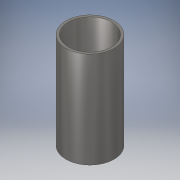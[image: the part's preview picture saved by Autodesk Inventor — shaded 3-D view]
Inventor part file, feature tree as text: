
AUTODESK INVENTOR PART (.ipt)
format: ipt  version: 2018 (Build 220112000, 112)  size: 103,424 bytes
history: native  units: in
note: dims shown in document units (in); Inventor stores cm internally (conversion verified against a paired STEP export)
features: extrude x1, sketch x1
ambient origin geometry x8: Origin, YZ Plane, XZ Plane, XY Plane, X Axis, Y Axis, Z Axis, Center Point
bodies: Solid1 (feature_tree)
feature tree (2):
  extrude  "Extrusion1"  Depth=1.0in
  sketch  "Sketch1"  dims[d0=0.5in d1=0.025in d2=1.0in d3=0.0in]
